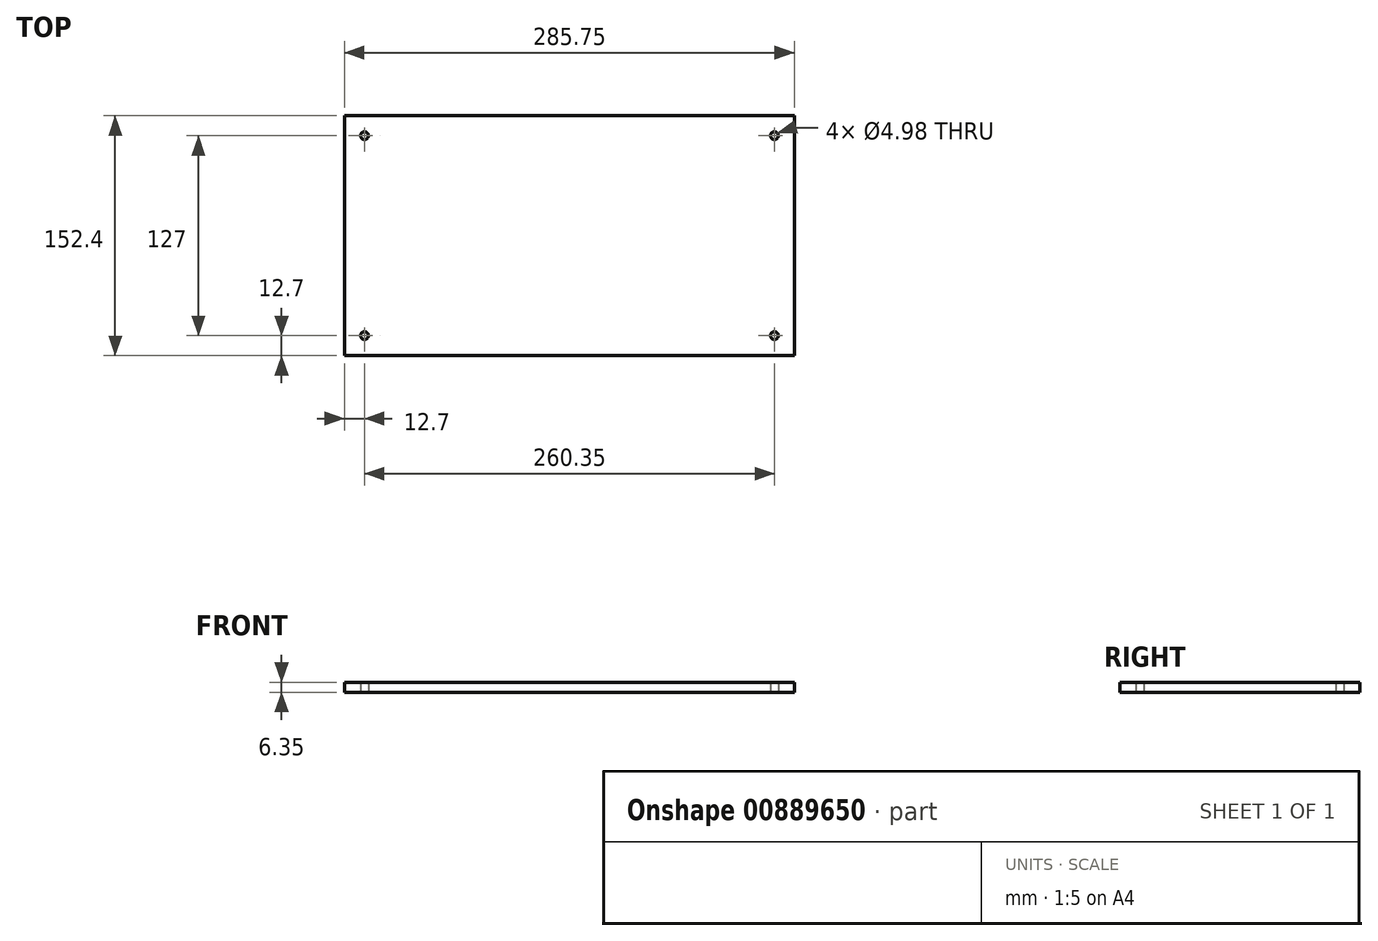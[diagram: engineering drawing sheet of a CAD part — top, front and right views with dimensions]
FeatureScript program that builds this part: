
annotation { "Feature Type Name" : "Feature", "Feature Type Description" : "" }
export const myFeature = defineFeature(function(context is Context, id is Id, definition is map)
    precondition{}
    {
        {
            var Q0;
            Q0=qCreatedBy(makeId("Top.planeOp"),FACE);
            var sketch = newSketch(context, id + "F0", { "sketchPlane" : qUnion([Q0])});
            skLineSegment(sketch, "E0.bottom", {"start": v(0, 0) * mm, "end": v(285.75, 0) * mm});
            skLineSegment(sketch, "E0.top", {"start": v(0, 152.4) * mm, "end": v(285.75, 152.4) * mm});
            skLineSegment(sketch, "E0.left", {"start": v(0, 0) * mm, "end": v(0, 152.4) * mm});
            skLineSegment(sketch, "E0.right", {"start": v(285.75, 0) * mm, "end": v(285.75, 152.4) * mm});
            skCircle(sketch, "E1", {"center": v(12.7, 12.7) * mm, "radius": 2.49 * mm});
            skCircle(sketch, "E2.0.1.0", {"center": v(12.7, 139.7) * mm, "radius": 2.49 * mm});
            skCircle(sketch, "E2.1.0.0", {"center": v(273.05, 12.7) * mm, "radius": 2.49 * mm});
            skCircle(sketch, "E2.1.1.0", {"center": v(273.05, 139.7) * mm, "radius": 2.49 * mm});
            skLineSegment(sketch, "E2.direction1", {"start": v(12.7, 12.7) * mm, "end": v(273.05, 12.7) * mm, "construction": true});
            skLineSegment(sketch, "E2.direction2", {"start": v(12.7, 12.7) * mm, "end": v(12.7, 139.7) * mm, "construction": true});
            skSolve(sketch);
        }
        {
            var Q0;
            Q0=makeQuery(id+"F0.imprint","IMPRINT",FACE,{"disambiguationData":[TD([[makeQuery(id+"F0.imprint","IMPRINT",EDGE,{"derivedFrom":sQuery(id+"F0.wireOp",EDGE,"E0.bottom")}),1.0]])]});
            extrude(context, id + "F1", {"entities" : qUnion([Q0]), "depth" : 6.35 * mm, "offsetDistance" : 25.4 * mm});
        }
    });
